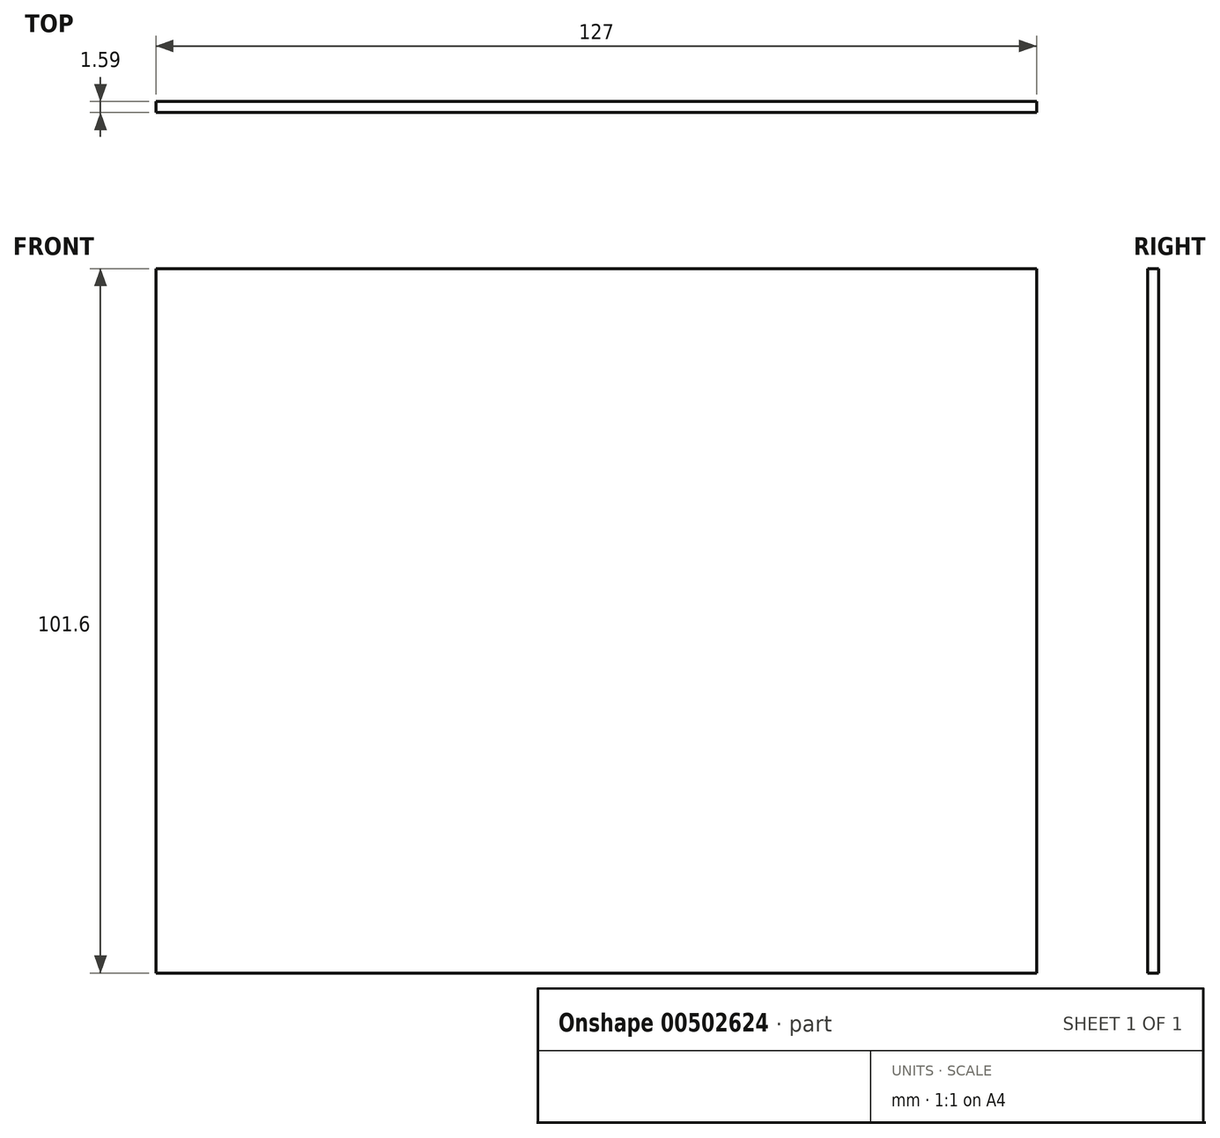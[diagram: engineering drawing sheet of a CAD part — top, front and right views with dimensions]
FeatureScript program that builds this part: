
annotation { "Feature Type Name" : "Feature", "Feature Type Description" : "" }
export const myFeature = defineFeature(function(context is Context, id is Id, definition is map)
    precondition{}
    {
        {
            var Q0;
            Q0=qCreatedBy(makeId("Front.planeOp"),FACE);
            var sketch = newSketch(context, id + "F0", { "sketchPlane" : qUnion([Q0])});
            skLineSegment(sketch, "E0.bottom", {"start": v(0, 0) * mm, "end": v(127, 0) * mm});
            skLineSegment(sketch, "E0.top", {"start": v(0, 101.6) * mm, "end": v(127, 101.6) * mm});
            skLineSegment(sketch, "E0.left", {"start": v(0, 0) * mm, "end": v(0, 101.6) * mm});
            skLineSegment(sketch, "E0.right", {"start": v(127, 0) * mm, "end": v(127, 101.6) * mm});
            skSolve(sketch);
        }
        {
            var Q0;
            Q0=makeQuery(id+"F0.imprint","IMPRINT",FACE,{"disambiguationData":[TD([[makeQuery(id+"F0.imprint","IMPRINT",EDGE,{"derivedFrom":sQuery(id+"F0.wireOp",EDGE,"E0.bottom")}),1.0]])]});
            extrude(context, id + "F1", {"entities" : qUnion([Q0]), "depth" : 1.59 * mm});
        }
    });
